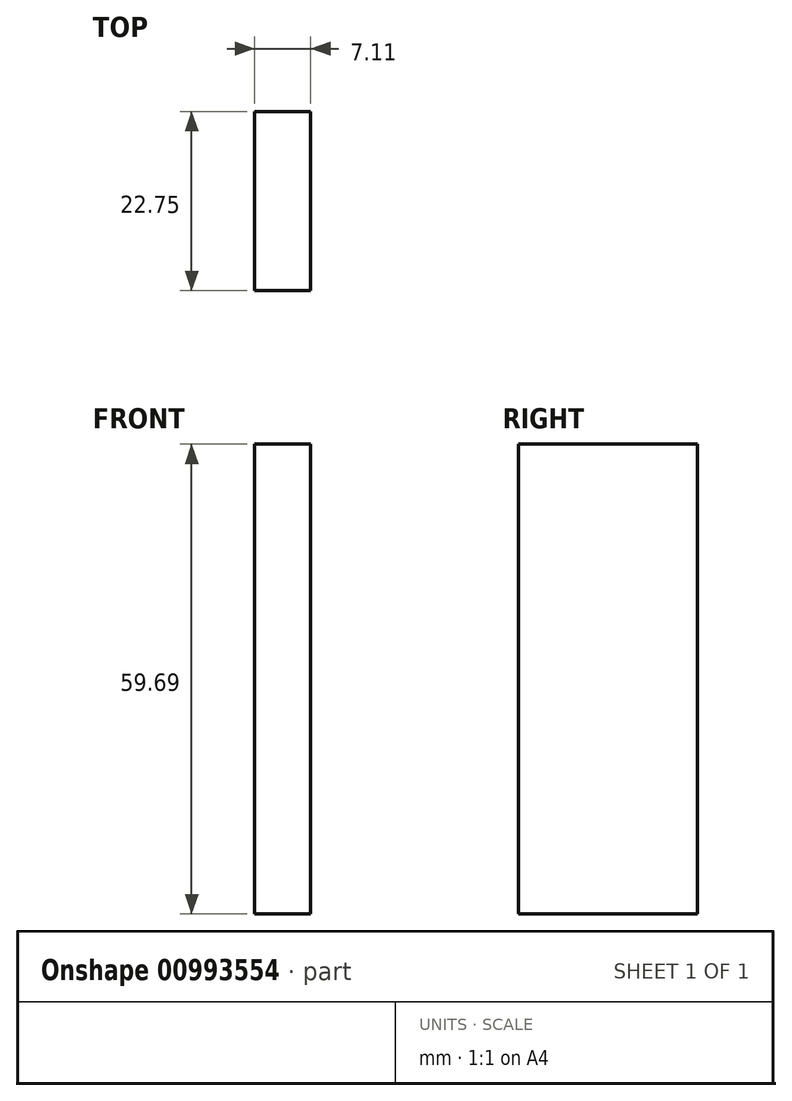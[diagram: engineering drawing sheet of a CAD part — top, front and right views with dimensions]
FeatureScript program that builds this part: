
annotation { "Feature Type Name" : "Feature", "Feature Type Description" : "" }
export const myFeature = defineFeature(function(context is Context, id is Id, definition is map)
    precondition{}
    {
        {
            var Q0;
            Q0=qCreatedBy(makeId("Top.planeOp"),FACE);
            var sketch = newSketch(context, id + "F0", { "sketchPlane" : qUnion([Q0])});
            skLineSegment(sketch, "E0.bottom", {"start": v(53.82, 42.39) * mm, "end": v(60.93, 42.39) * mm});
            skLineSegment(sketch, "E0.top", {"start": v(53.82, 65.14) * mm, "end": v(60.93, 65.14) * mm});
            skLineSegment(sketch, "E0.left", {"start": v(53.82, 42.39) * mm, "end": v(53.82, 65.14) * mm});
            skLineSegment(sketch, "E0.right", {"start": v(60.93, 42.39) * mm, "end": v(60.93, 65.14) * mm});
            skSolve(sketch);
        }
        {
            var Q0;
            Q0 = qSketchRegion(id + "F0", true);
            extrude(context, id + "F1", {"entities" : qUnion([Q0]), "depth" : 59.69 * mm, "offsetDistance" : 25.4 * mm});
        }
    });
